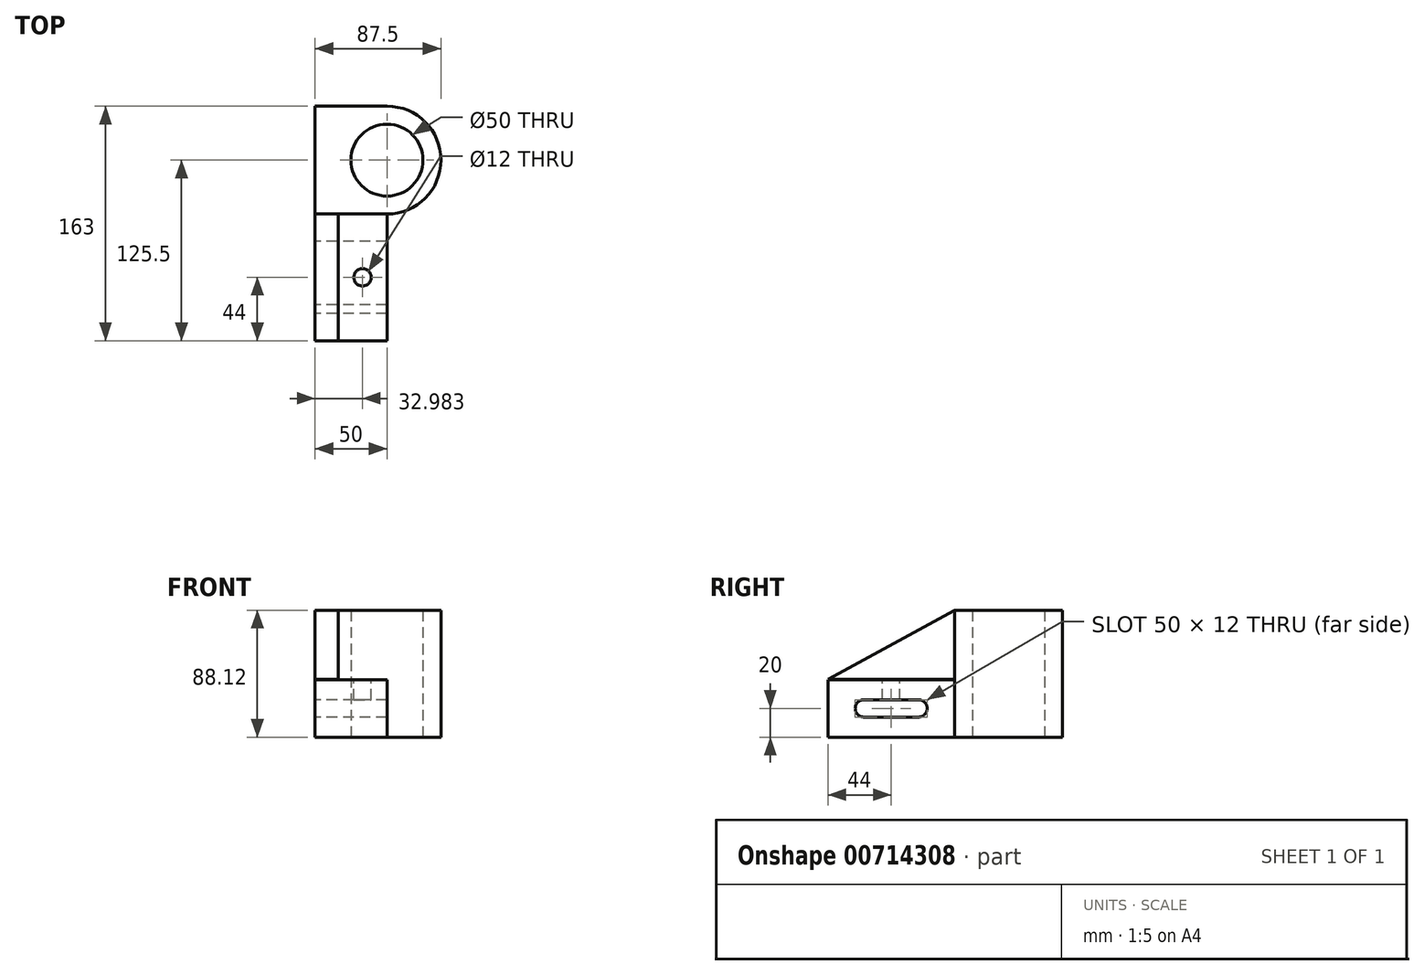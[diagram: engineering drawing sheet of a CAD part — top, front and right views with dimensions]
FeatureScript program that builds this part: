
annotation { "Feature Type Name" : "Feature", "Feature Type Description" : "" }
export const myFeature = defineFeature(function(context is Context, id is Id, definition is map)
    precondition{}
    {
        {
            var Q0;
            Q0=qCreatedBy(makeId("Top.planeOp"),FACE);
            var sketch = newSketch(context, id + "F0", { "sketchPlane" : qUnion([Q0])});
            skLineSegment(sketch, "E0.bottom", {"start": v(0, 0) * mm, "end": v(50, 0) * mm});
            skLineSegment(sketch, "E0.top", {"start": v(0, 75) * mm, "end": v(50, 75) * mm});
            skLineSegment(sketch, "E0.left", {"start": v(0, 0) * mm, "end": v(0, 75) * mm});
            skArc(sketch, "E1", {"start": v(50, 0) * mm, "mid": v(87.5, 37.5) * mm, "end": v(50, 75) * mm});
            skCircle(sketch, "E2", {"center": v(50, 37.5) * mm, "radius": 25 * mm});
            skSolve(sketch);
        }
        {
            var Q0;
            Q0 = qSketchRegion(id + "F0", true);
            extrude(context, id + "F1", {"entities" : qUnion([Q0]), "depth" : 88 * mm, "offsetDistance" : 25 * mm});
        }
        {
            var Q0;
            Q0=qCreatedBy(makeId("Right.planeOp"),FACE);
            var sketch = newSketch(context, id + "F2", { "sketchPlane" : qUnion([Q0])});
            skLineSegment(sketch, "E3.bottom", {"start": v(0, 0) * mm, "end": v(-88, 0) * mm});
            skLineSegment(sketch, "E3.top", {"start": v(0, 40) * mm, "end": v(-88, 40) * mm});
            skLineSegment(sketch, "E3.left", {"start": v(0, 0) * mm, "end": v(0, 40) * mm});
            skLineSegment(sketch, "E3.right", {"start": v(-88, 0) * mm, "end": v(-88, 40) * mm});
            skArc(sketch, "E4", {"start": v(-62.92, 26) * mm, "mid": v(-69, 20) * mm, "end": v(-62.92, 14) * mm});
            skArc(sketch, "E5", {"start": v(-25, 14) * mm, "mid": v(-19, 20) * mm, "end": v(-25, 26) * mm});
            skLineSegment(sketch, "E6", {"start": v(-62.92, 26) * mm, "end": v(-25, 26) * mm});
            skLineSegment(sketch, "E7", {"start": v(-62.92, 14) * mm, "end": v(-25, 14) * mm});
            skSolve(sketch);
        }
        {
            var Q0;
            Q0 = qSketchRegion(id + "F2", true);
            extrude(context, id + "F3", {"entities" : qUnion([Q0]), "operationType" : NewBodyOperationType.ADD, "depth" : 50 * mm, "offsetDistance" : 25 * mm});
        }
        {
            var Q0;
            Q0=qCreatedBy(makeId("Right.planeOp"),FACE);
            var sketch = newSketch(context, id + "F4", { "sketchPlane" : qUnion([Q0])});
            skLineSegment(sketch, "E8", {"start": v(-88, 40.12) * mm, "end": v(0, 40.12) * mm});
            skLineSegment(sketch, "E9", {"start": v(0, 40.12) * mm, "end": v(0, 88.12) * mm});
            skLineSegment(sketch, "E10", {"start": v(-88, 40.12) * mm, "end": v(0, 88.12) * mm});
            skSolve(sketch);
        }
        {
            var Q0;
            Q0 = qSketchRegion(id + "F4", true);
            extrude(context, id + "F5", {"entities" : qUnion([Q0]), "operationType" : NewBodyOperationType.ADD, "depth" : 16 * mm, "offsetDistance" : 25 * mm});
        }
        {
            var Q0;
            Q0=makeQuery(id+"F3.opExtrude","SWEPT_FACE",FACE,{"disambiguationData":[OSD([sQuery(id+"F2.wireOp",EDGE,"E3.top")])]});
            var sketch = newSketch(context, id + "F6", { "sketchPlane" : qUnion([Q0])});
            skCircle(sketch, "E11", {"center": v(32.98, -44) * mm, "radius": 6 * mm});
            skSolve(sketch);
        }
        {
            var Q0;
            Q0=makeQuery(id+"F6.imprint","IMPRINT",FACE,{"disambiguationData":[TD([[makeQuery(id+"F6.imprint","IMPRINT",EDGE,{"derivedFrom":sQuery(id+"F6.wireOp",EDGE,"E11")}),1.0]])]});
            extrude(context, id + "F7", {"entities" : qUnion([Q0]), "operationType" : NewBodyOperationType.REMOVE, "endBound" : BoundingType.UP_TO_NEXT, "oppositeDirection" : true, "depth" : 25 * mm, "offsetDistance" : 25 * mm});
        }
    });
